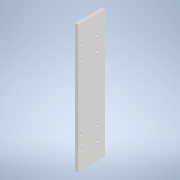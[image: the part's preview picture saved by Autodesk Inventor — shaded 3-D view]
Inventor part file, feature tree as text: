
AUTODESK INVENTOR PART (.ipt)
format: ipt  version: 2022 (Build 260153000, 153)  size: 122,880 bytes
history: native  units: mm
features: sketch x2, other x1, extrude x1, hole x1
ambient origin geometry x8: Origin, YZ Plane, XZ Plane, XY Plane, X Axis, Y Axis, Z Axis, Center Point
bodies: Body1 (feature_tree)
feature tree (5):
  other  "ソリッド1"
  extrude  "押し出し1"  Depth=40.0mm
  hole  "穴1"  [1 undecoded]
  sketch  "スケッチ1"
  sketch  "スケッチ2"
note: 1 required parameter value undecoded (feature->parameter linkage not recoverable at this tier; creation-order binding heuristic only, values carry confidence <= 0.55)
